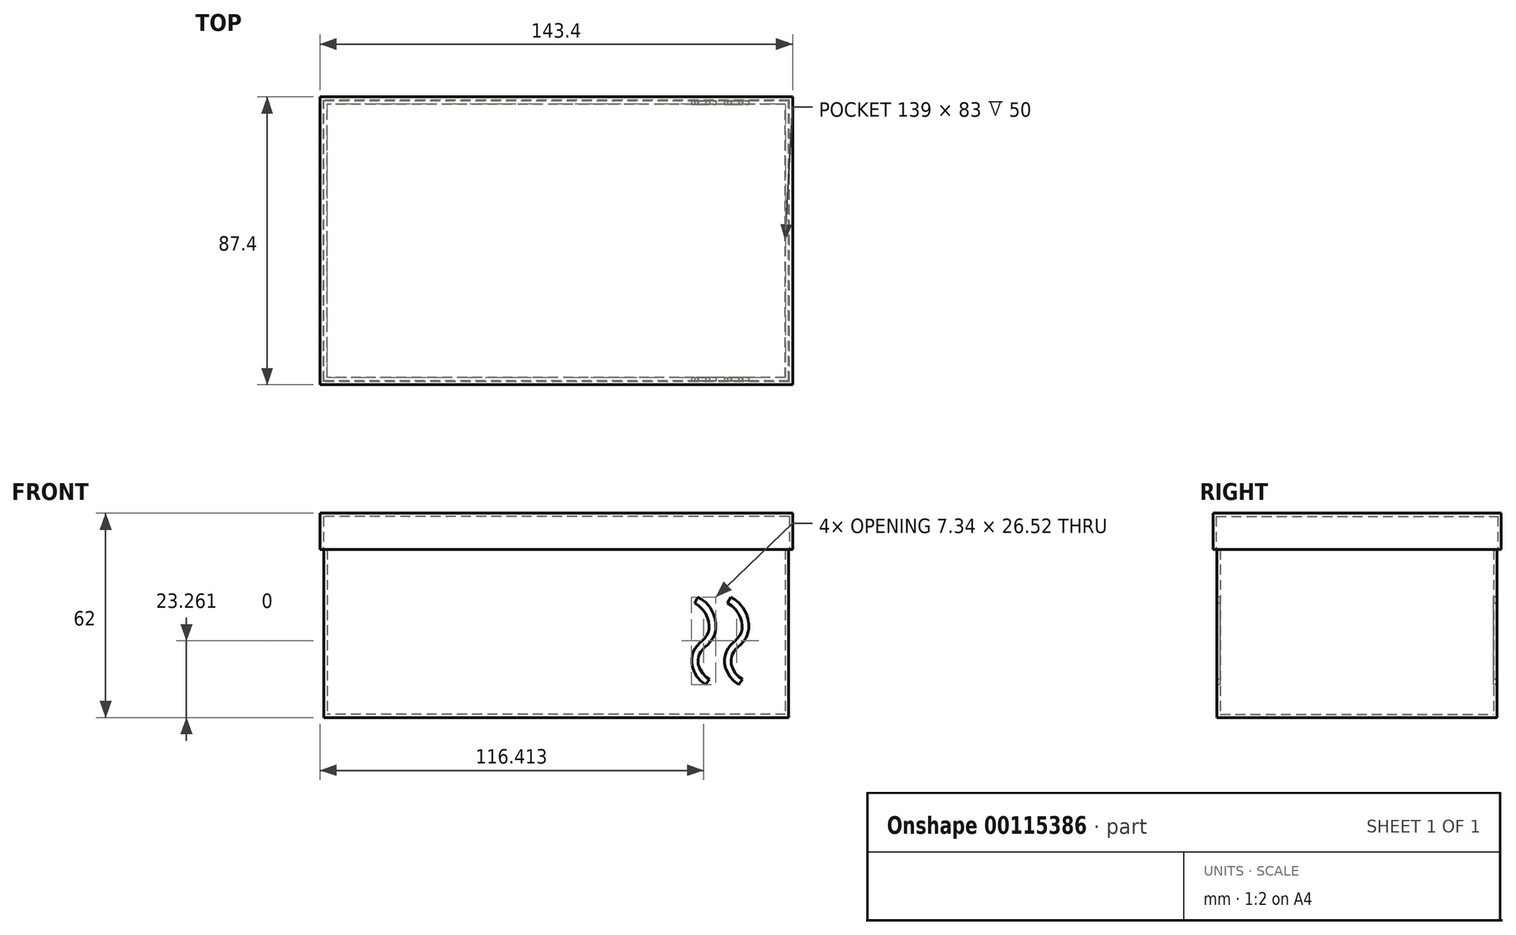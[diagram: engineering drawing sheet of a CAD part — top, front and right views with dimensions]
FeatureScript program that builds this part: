
annotation { "Feature Type Name" : "Feature", "Feature Type Description" : "" }
export const myFeature = defineFeature(function(context is Context, id is Id, definition is map)
    precondition{}
    {
        {
            var Q0;
            Q0=qCreatedBy(makeId("Top.planeOp"),FACE);
            var sketch = newSketch(context, id + "F0", { "sketchPlane" : qUnion([Q0])});
            skLineSegment(sketch, "E0.bottom", {"start": v(70.5, -42.5) * mm, "end": v(-70.5, -42.5) * mm});
            skLineSegment(sketch, "E0.top", {"start": v(70.5, 42.5) * mm, "end": v(-70.5, 42.5) * mm});
            skLineSegment(sketch, "E0.left", {"start": v(70.5, -42.5) * mm, "end": v(70.5, 42.5) * mm});
            skLineSegment(sketch, "E0.right", {"start": v(-70.5, -42.5) * mm, "end": v(-70.5, 42.5) * mm});
            skPoint(sketch, "E0.middle", {"position": v(0, 0) * mm});
            skSolve(sketch);
        }
        {
            var Q0;
            Q0 = qSketchRegion(id + "F0", true);
            extrude(context, id + "F1", {"entities" : qUnion([Q0]), "depth" : 51 * mm});
        }
        {
            var Q0;
            Q0=makeQuery(id+"F1.opExtrude","CAP_FACE",FACE,{"disambiguationData":[OSD([sQuery(id+"F0.wireOp",EDGE,"E0.bottom"),sQuery(id+"F0.wireOp",EDGE,"E0.top"),sQuery(id+"F0.wireOp",EDGE,"E0.left"),sQuery(id+"F0.wireOp",EDGE,"E0.right")])],"isStart":false});
            shell(context, id + "F2", {"entities" : qUnion([Q0]), "thickness" : 1 * mm});
        }
        {
            var Q0;
            Q0=makeQuery(id+"F1.opExtrude","SWEPT_FACE",FACE,{"disambiguationData":[OSD([sQuery(id+"F0.wireOp",EDGE,"E0.bottom")])]});
            var sketch = newSketch(context, id + "F3", { "sketchPlane" : qUnion([Q0])});
            skFitSpline(sketch, "E1", {"points": [v(45.33, 10) * mm, v(41.88, 20.59) * mm, v(46.05, 25.72) * mm, v(41.96, 34.79) * mm], "startDerivative": vector(-38.83, 25.87) * mm, "endDerivative": vector(-34.2, 19.55) * mm});
            skFitSpline(sketch, "E2", {"points": [v(55.33, 10) * mm, v(51.88, 20.59) * mm, v(56.05, 25.72) * mm, v(51.96, 34.79) * mm], "startDerivative": vector(-38.83, 25.87) * mm, "endDerivative": vector(-34.2, 19.55) * mm});
            skLineSegment(sketch, "E3", {"start": v(45.33, 10) * mm, "end": v(55.33, 10) * mm, "construction": true});
            skLineSegment(sketch, "E4", {"start": v(41.96, 34.79) * mm, "end": v(51.96, 34.79) * mm, "construction": true});
            skFitSpline(sketch, "E5.0", {"points": [v(46.44, 11.66) * mm, v(45.75, 12.12) * mm, v(44.65, 13.08) * mm, v(43.63, 14.55) * mm, v(43.1, 16.01) * mm, v(43, 17.19) * mm, v(43.1, 18.07) * mm, v(43.23, 18.68) * mm, v(43.4, 19.15) * mm, v(43.56, 19.48) * mm, v(43.73, 19.8) * mm, v(43.98, 20.16) * mm, v(44.35, 20.6) * mm, v(44.8, 21.06) * mm, v(45.47, 21.7) * mm, v(46.24, 22.43) * mm, v(47.01, 23.35) * mm, v(47.46, 24.03) * mm, v(47.77, 24.64) * mm, v(47.97, 25.13) * mm, v(48.14, 25.65) * mm, v(48.3, 26.35) * mm, v(48.4, 27.25) * mm, v(48.38, 28.72) * mm, v(48, 30.6) * mm, v(46.96, 32.84) * mm, v(45.32, 34.89) * mm, v(43.8, 36.03) * mm, v(42.95, 36.52) * mm]});
            skFitSpline(sketch, "E6.0", {"points": [v(56.44, 11.66) * mm, v(55.75, 12.12) * mm, v(54.65, 13.08) * mm, v(53.63, 14.55) * mm, v(53.1, 16.01) * mm, v(53, 17.19) * mm, v(53.1, 18.07) * mm, v(53.23, 18.68) * mm, v(53.4, 19.15) * mm, v(53.56, 19.48) * mm, v(53.73, 19.8) * mm, v(53.98, 20.16) * mm, v(54.35, 20.6) * mm, v(54.8, 21.06) * mm, v(55.47, 21.7) * mm, v(56.24, 22.43) * mm, v(57.01, 23.35) * mm, v(57.46, 24.03) * mm, v(57.77, 24.64) * mm, v(57.97, 25.13) * mm, v(58.14, 25.65) * mm, v(58.3, 26.35) * mm, v(58.4, 27.25) * mm, v(58.38, 28.72) * mm, v(58, 30.6) * mm, v(56.96, 32.84) * mm, v(55.32, 34.89) * mm, v(53.8, 36.03) * mm, v(52.95, 36.52) * mm]});
            skLineSegment(sketch, "E7", {"start": v(41.96, 34.79) * mm, "end": v(42.95, 36.52) * mm});
            skLineSegment(sketch, "E8", {"start": v(51.96, 34.79) * mm, "end": v(52.95, 36.52) * mm});
            skLineSegment(sketch, "E9", {"start": v(45.33, 10) * mm, "end": v(46.44, 11.66) * mm});
            skLineSegment(sketch, "E10", {"start": v(55.33, 10) * mm, "end": v(56.44, 11.66) * mm});
            skSolve(sketch);
        }
        {
            var Q0;
            Q0 = qSketchRegion(id + "F3", true);
            var Q1;
            Q1=makeQuery(id+"F1.opExtrude","SWEPT_FACE",FACE,{"disambiguationData":[OSD([sQuery(id+"F0.wireOp",EDGE,"E0.top")])]});
            extrude(context, id + "F4", {"entities" : qUnion([Q0]), "operationType" : NewBodyOperationType.REMOVE, "endBound" : BoundingType.UP_TO_SURFACE, "oppositeDirection" : true, "endBoundEntityFace" : qUnion([Q1]), "depth" : 25 * mm});
        }
        {
            var Q0;
            Q0=makeQuery(id+"F1.opExtrude","CAP_FACE",FACE,{"disambiguationData":[OSD([sQuery(id+"F0.wireOp",EDGE,"E0.bottom"),sQuery(id+"F0.wireOp",EDGE,"E0.top"),sQuery(id+"F0.wireOp",EDGE,"E0.left"),sQuery(id+"F0.wireOp",EDGE,"E0.right")])],"isStart":false});
            var sketch = newSketch(context, id + "F5", { "sketchPlane" : qUnion([Q0])});
            skLineSegment(sketch, "E11.0", {"start": v(70.7, -42.7) * mm, "end": v(70.7, 42.7) * mm});
            skLineSegment(sketch, "E11.1", {"start": v(70.7, -42.7) * mm, "end": v(-70.7, -42.7) * mm});
            skLineSegment(sketch, "E11.2", {"start": v(-70.7, -42.7) * mm, "end": v(-70.7, 42.7) * mm});
            skLineSegment(sketch, "E11.3", {"start": v(70.7, 42.7) * mm, "end": v(-70.7, 42.7) * mm});
            skLineSegment(sketch, "E12.0", {"start": v(71.7, -43.7) * mm, "end": v(71.7, 43.7) * mm});
            skLineSegment(sketch, "E12.1", {"start": v(71.7, -43.7) * mm, "end": v(-71.7, -43.7) * mm});
            skLineSegment(sketch, "E12.2", {"start": v(-71.7, -43.7) * mm, "end": v(-71.7, 43.7) * mm});
            skLineSegment(sketch, "E12.3", {"start": v(71.7, 43.7) * mm, "end": v(-71.7, 43.7) * mm});
            skSolve(sketch);
        }
        {
            var Q0;
            Q0 = qSketchRegion(id + "F5", true);
            extrude(context, id + "F6", {"entities" : qUnion([Q0]), "depth" : 10 * mm});
        }
        {
            var Q0;
            Q0=makeQuery(id+"F6.opExtrude","CAP_FACE",FACE,{"disambiguationData":[OSD([sQuery(id+"F5.wireOp",EDGE,"E11.0"),sQuery(id+"F5.wireOp",EDGE,"E11.1"),sQuery(id+"F5.wireOp",EDGE,"E11.2"),sQuery(id+"F5.wireOp",EDGE,"E11.3"),sQuery(id+"F5.wireOp",EDGE,"E12.0"),sQuery(id+"F5.wireOp",EDGE,"E12.1"),sQuery(id+"F5.wireOp",EDGE,"E12.2"),sQuery(id+"F5.wireOp",EDGE,"E12.3")])],"isStart":false});
            var sketch = newSketch(context, id + "F7", { "sketchPlane" : qUnion([Q0])});
            skLineSegment(sketch, "E13.bottom", {"start": v(71.7, -43.7) * mm, "end": v(-71.7, -43.7) * mm});
            skLineSegment(sketch, "E13.top", {"start": v(71.7, 43.7) * mm, "end": v(-71.7, 43.7) * mm});
            skLineSegment(sketch, "E13.left", {"start": v(71.7, -43.7) * mm, "end": v(71.7, 43.7) * mm});
            skLineSegment(sketch, "E13.right", {"start": v(-71.7, -43.7) * mm, "end": v(-71.7, 43.7) * mm});
            skSolve(sketch);
        }
        {
            var Q0;
            Q0 = qSketchRegion(id + "F7", true);
            extrude(context, id + "F8", {"entities" : qUnion([Q0]), "operationType" : NewBodyOperationType.ADD, "depth" : 1 * mm});
        }
    });
